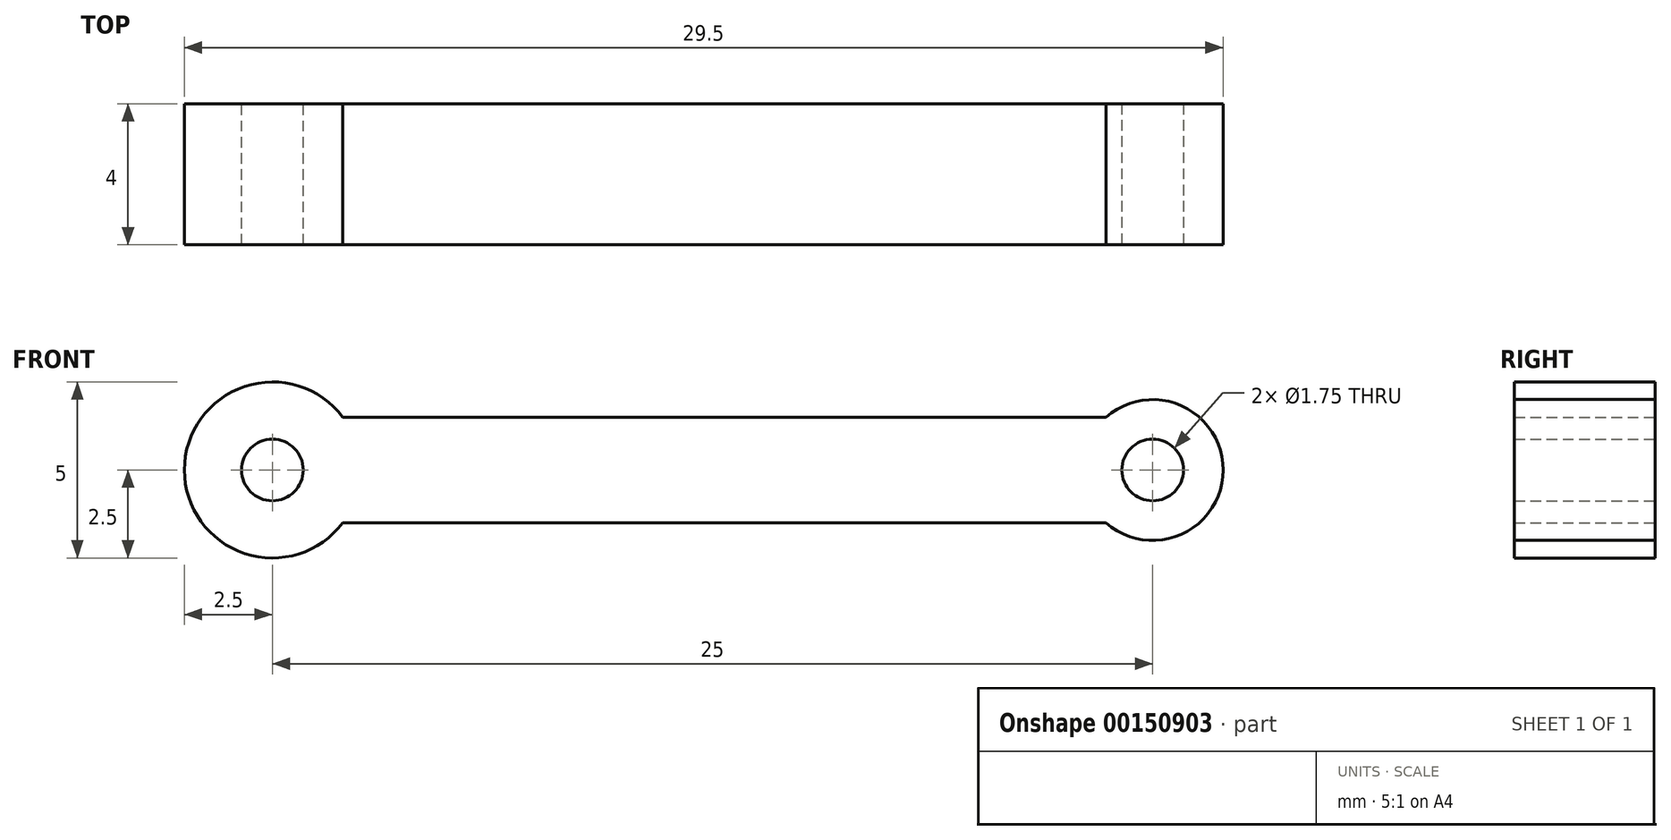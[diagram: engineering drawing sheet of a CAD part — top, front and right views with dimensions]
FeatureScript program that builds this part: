
annotation { "Feature Type Name" : "Feature", "Feature Type Description" : "" }
export const myFeature = defineFeature(function(context is Context, id is Id, definition is map)
    precondition{}
    {
        {
            var Q0;
            Q0=qCreatedBy(makeId("Front.planeOp"),FACE);
            var sketch = newSketch(context, id + "F0", { "sketchPlane" : qUnion([Q0])});
            skCircle(sketch, "E0", {"center": v(-12.5, 0) * mm, "radius": 0.87 * mm});
            skLineSegment(sketch, "E1.bottom", {"start": v(-10.5, -1.5) * mm, "end": v(11.18, -1.5) * mm});
            skLineSegment(sketch, "E1.top", {"start": v(-10.5, 1.5) * mm, "end": v(11.18, 1.5) * mm});
            skArc(sketch, "E2", {"start": v(-10.5, 1.5) * mm, "mid": v(-15, 0) * mm, "end": v(-10.5, -1.5) * mm});
            skCircle(sketch, "E3", {"center": v(12.5, 0) * mm, "radius": 2 * mm});
            skLineSegment(sketch, "E4", {"start": v(11.18, 1.5) * mm, "end": v(11.18, -1.5) * mm});
            skSolve(sketch);
        }
        {
            var Q0;
            Q0=qSketchRegion(id+"F0",true);
            extrude(context, id + "F1", {"entities" : qUnion([Q0]), "endBound" : BoundingType.SYMMETRIC, "depth" : 4 * mm});
        }
        {
            var Q0;
            Q0=makeQuery(id+"F1.opExtrude","CAP_FACE",FACE,{"disambiguationData":[OSD([sQuery(id+"F0.wireOp",EDGE,"E0"),sQuery(id+"F0.wireOp",EDGE,"E1.bottom"),sQuery(id+"F0.wireOp",EDGE,"E1.top"),sQuery(id+"F0.wireOp",EDGE,"E2"),sQuery(id+"F0.wireOp",EDGE,"E3"),sQuery(id+"F0.wireOp",EDGE,"E4")])],"isStart":false});
            var sketch = newSketch(context, id + "F2", { "sketchPlane" : qUnion([Q0])});
            skCircle(sketch, "E5", {"center": v(12.5, 0) * mm, "radius": 0.88 * mm});
            skSolve(sketch);
        }
        {
            var Q0;
            Q0=qSketchRegion(id+"F2",true);
            extrude(context, id + "F3", {"entities" : qUnion([Q0]), "operationType" : NewBodyOperationType.REMOVE, "endBound" : BoundingType.THROUGH_ALL, "oppositeDirection" : true, "depth" : 25 * mm});
        }
    });
